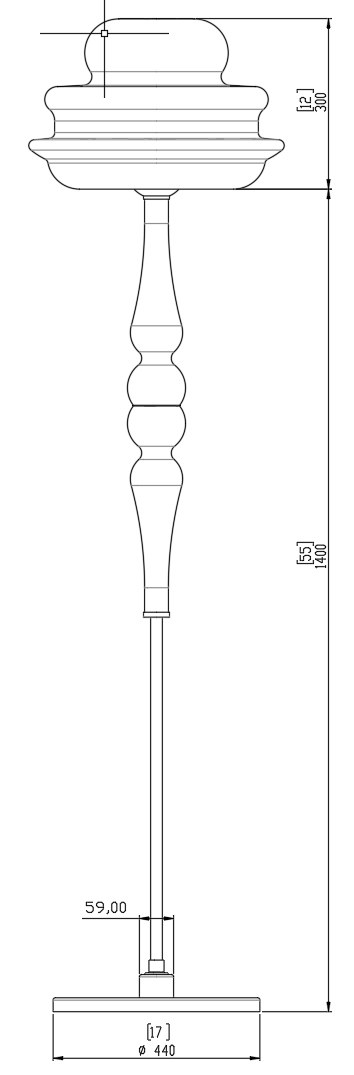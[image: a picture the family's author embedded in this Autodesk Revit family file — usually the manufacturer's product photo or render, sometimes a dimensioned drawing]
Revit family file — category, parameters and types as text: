
# Revit family: PEGGY SP-Suspension
name_source: partatom
category: Lighting Fixtures
units: mm (PartAtom-declared; Revit-internal decimal feet)

## family parameters
Always vertical = Yes
Cut with Voids When Loaded = No
Host = Ceiling
Light Source = No
OmniClass Number = 23.80.70.11
OmniClass Title = Luminaries for Internal Lighting
Part Type = Normal
Room Calculation Point = No
Round Connector Dimension = Use Diameter
Shared = No

## types (1)
- PEGGY SP
    Bulb Diametr = 15 mm  [stored 0.0492126 ft]
    Country = Europe
    Default Elevation = 0 mm  [stored 0 ft]
    Depth = 0 mm  [stored 0 ft]
    Description = SUSPENSION
    Designer = Hangar Design Group
    Frame finish = <By Category>
    Glass finish_type1 = <By Category>
    Manufacturer = Vistosi
    Manufacturer country = Italy
    Material Bulb = 000_VISTOSI_Bulb
    Model = PEGGY
    Type Comments = Hangar Design Group
    URL = https://vistosi.com
    URL Product Page = https://vistosi.it
    Width = 22 mm

note: [stored X ft] marks values corroborated as IEEE doubles in the binary element streams (Revit-internal decimal feet)

## geometry (parser evidence)
native form markers: Sweep x11
no freeform markers — native parametric forms only
